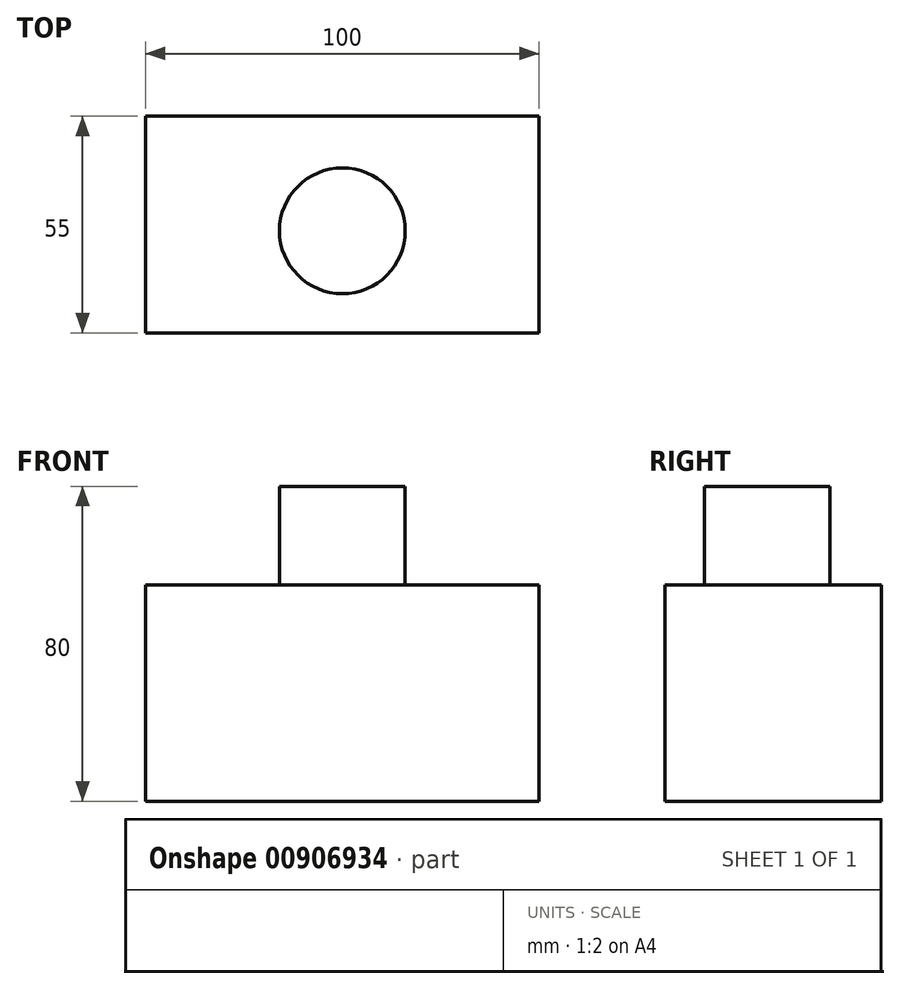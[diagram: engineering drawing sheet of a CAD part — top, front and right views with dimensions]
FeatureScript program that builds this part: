
annotation { "Feature Type Name" : "Feature", "Feature Type Description" : "" }
export const myFeature = defineFeature(function(context is Context, id is Id, definition is map)
    precondition{}
    {
        {
            var Q0;
            Q0=qCreatedBy(makeId("Front.planeOp"),FACE);
            var sketch = newSketch(context, id + "F0", { "sketchPlane" : qUnion([Q0])});
            skLineSegment(sketch, "E0.bottom", {"start": v(-50, 40) * mm, "end": v(50, 40) * mm});
            skLineSegment(sketch, "E0.top", {"start": v(-50, -40) * mm, "end": v(50, -40) * mm});
            skLineSegment(sketch, "E0.left", {"start": v(-50, 40) * mm, "end": v(-50, -40) * mm});
            skLineSegment(sketch, "E0.right", {"start": v(50, 40) * mm, "end": v(50, -40) * mm});
            skPoint(sketch, "E0.middle", {"position": v(0, 0) * mm});
            skSolve(sketch);
        }
        {
            var Q0;
            Q0 = qSketchRegion(id + "F0", true);
            extrude(context, id + "F1", {"entities" : qUnion([Q0]), "depth" : 55 * mm, "offsetDistance" : 25 * mm});
        }
        {
            var Q0;
            Q0=makeQuery(id+"F1.opExtrude","SWEPT_FACE",FACE,{"disambiguationData":[OSD([sQuery(id+"F0.wireOp",EDGE,"E0.bottom")])]});
            var sketch = newSketch(context, id + "F2", { "sketchPlane" : qUnion([Q0])});
            skCircle(sketch, "E1", {"center": v(0, -29.09) * mm, "radius": 15.98 * mm});
            skSolve(sketch);
        }
        {
            var Q0;
            Q0=makeQuery(id+"F2.imprint","IMPRINT",FACE,{"disambiguationData":[TD([[makeQuery(id+"F2.imprint","IMPRINT",EDGE,{"derivedFrom":sQuery(id+"F2.wireOp",EDGE,"E1")}),-1.0]])]});
            var Q1;
            Q1=sQuery(id+"F2.wireOp",EDGE,"E1");
            extrude(context, id + "F3", {"entities" : qUnion([Q0]), "operationType" : NewBodyOperationType.REMOVE, "surfaceEntities" : qUnion([Q1]), "oppositeDirection" : true, "depth" : 25 * mm, "offsetDistance" : 25 * mm});
        }
    });
